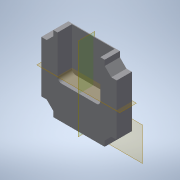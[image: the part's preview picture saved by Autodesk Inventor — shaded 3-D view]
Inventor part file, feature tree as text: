
AUTODESK INVENTOR PART (.ipt)
format: ipt  version: 2022 (Build 260153000, 153)  size: 230,912 bytes
history: native  units: mm
features: plane x5, extrude x4, sketch x4, projected_geometry x2
ambient origin geometry x8: Origin, YZ Plane, XZ Plane, XY Plane, X Axis, Y Axis, Z Axis, Center Point
bodies: Solid1 (feature_tree)
feature tree (15):
  plane  "Work Plane5"
  extrude  "Extrusion1"  Depth=10.0mm
  extrude  "IM_offset"  Depth=53.8mm
  extrude  "Extrusion23"  Depth=45.0mm
  extrude  "Extrusion24"  Depth=0.5mm
  plane  "Arbeitsebene7"
  plane  "Arbeitsebene8"
  plane  "Arbeitsebene9"
  plane  "Arbeitsebene10"
  sketch  "Sketch1"  dims[d10=10.0mm d11=0.0mm d18=53.8mm]
  sketch  "Skizze4"  dims[d19=45.0deg d20=53.8mm]
  projected_geometry  "Projizierte Kontur1"
  sketch  "Sketch29"  dims[d21=45.0mm d22=45.0mm]
  sketch  "Sketch30"  dims[d30=20.0mm d31=20.0mm d32=2.8mm d33=2.8mm d34=2.8mm d35=3.0mm d36=0.1mm d37=0.1mm d38=0.1mm d39=0.1mm d40=0.2mm d41=10.0mm d42=0.0mm d171=0.2mm d172=10.0mm d173=0.0mm d174=0.5mm d175=0.0mm]
  projected_geometry  "Projected Loop17"
